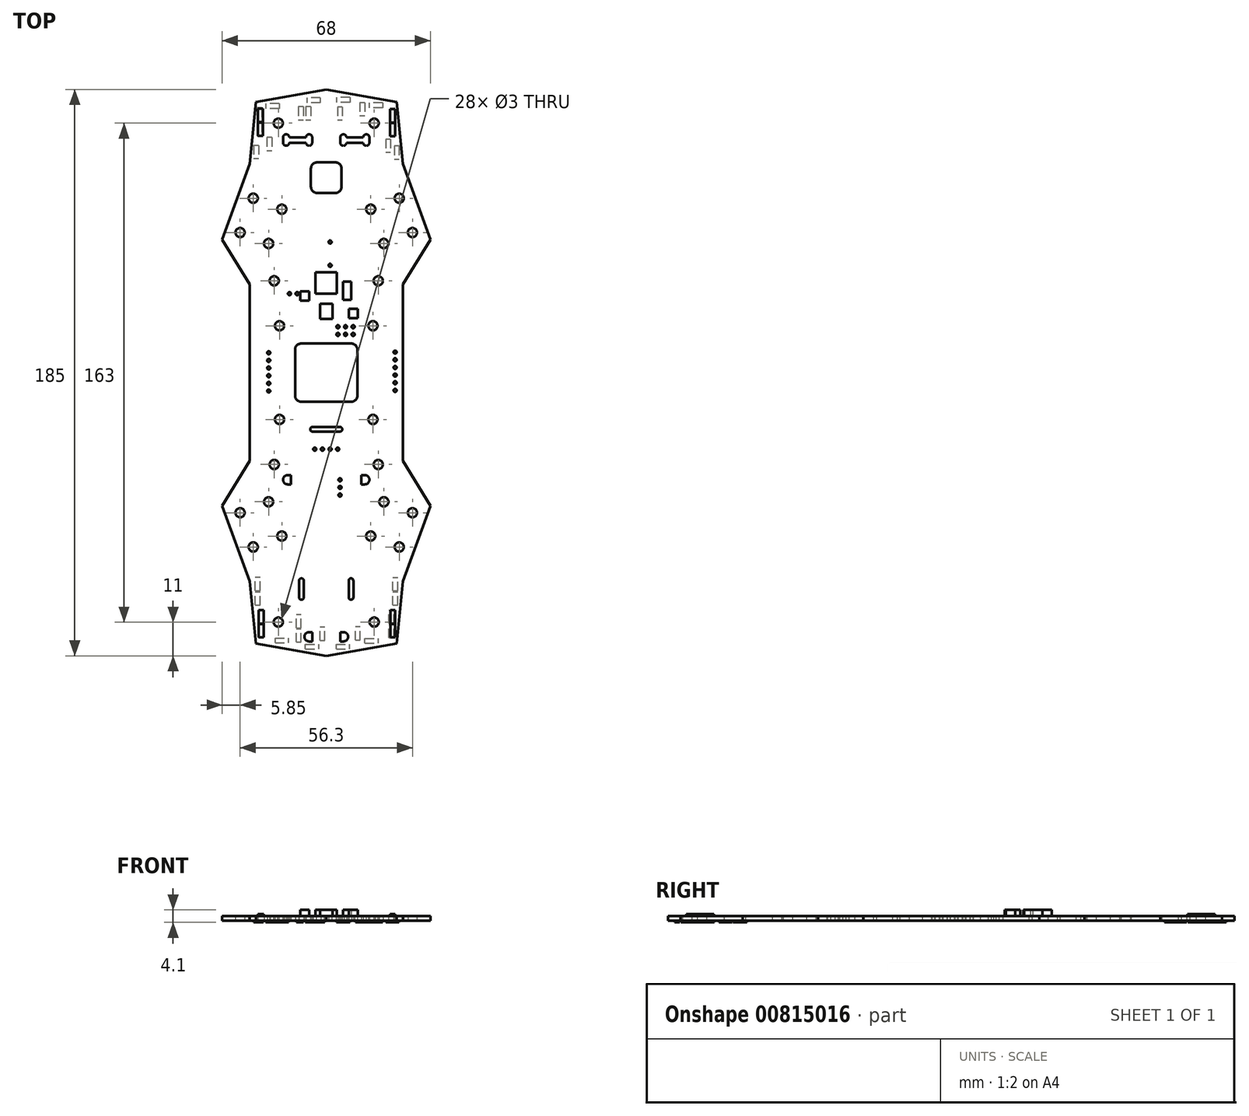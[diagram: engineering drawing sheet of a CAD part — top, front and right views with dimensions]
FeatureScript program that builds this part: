
annotation { "Feature Type Name" : "Feature", "Feature Type Description" : "" }
export const myFeature = defineFeature(function(context is Context, id is Id, definition is map)
    precondition{}
    {
        {
            var Q0;
            Q0=qCreatedBy(makeId("Top.planeOp"),FACE);
            var sketch = newSketch(context, id + "F0", { "sketchPlane" : qUnion([Q0])});
            skLineSegment(sketch, "E0.0.14", {"start": v(-25, 92.5) * mm, "end": v(-25, 63.7) * mm});
            skLineSegment(sketch, "E0.0.16", {"start": v(-25, 63.7) * mm, "end": v(-34, 49) * mm});
            skLineSegment(sketch, "E0.0.18", {"start": v(-34, 49) * mm, "end": v(-25, 24.3) * mm});
            skLineSegment(sketch, "E0.0.20", {"start": v(-25, 24.3) * mm, "end": v(-23, 4.06) * mm});
            skLineSegment(sketch, "E0.0.22", {"start": v(-23, 4.06) * mm, "end": v(0, 0) * mm});
            skLineSegment(sketch, "E0.0.23", {"start": v(0, 0) * mm, "end": v(23, 4.06) * mm});
            skLineSegment(sketch, "E0.0.25", {"start": v(23, 4.06) * mm, "end": v(25, 24.3) * mm});
            skLineSegment(sketch, "E0.0.27", {"start": v(25, 24.3) * mm, "end": v(34, 49) * mm});
            skLineSegment(sketch, "E0.0.29", {"start": v(34, 49) * mm, "end": v(25, 63.7) * mm});
            skLineSegment(sketch, "E0.0.31", {"start": v(25, 63.7) * mm, "end": v(25, 92.5) * mm});
            skLineSegment(sketch, "E1.bottom", {"start": v(34, 0) * mm, "end": v(-34, 0) * mm, "construction": true});
            skLineSegment(sketch, "E1.top", {"start": v(34, 185) * mm, "end": v(-34, 185) * mm, "construction": true});
            skLineSegment(sketch, "E1.left", {"start": v(-34, 0) * mm, "end": v(-34, 185) * mm, "construction": true});
            skLineSegment(sketch, "E1.right", {"start": v(34, 0) * mm, "end": v(34, 185) * mm, "construction": true});
            skPoint(sketch, "E2", {"position": v(0, 0) * mm});
            skLineSegment(sketch, "E3", {"start": v(0, 185) * mm, "end": v(0, 0) * mm, "construction": true});
            skLineSegment(sketch, "E4", {"start": v(-34, 92.5) * mm, "end": v(34, 92.5) * mm, "construction": true});
            skLineSegment(sketch, "E5.MirrorCS", {"start": v(-25, 92.5) * mm, "end": v(-25, 121.3) * mm});
            skLineSegment(sketch, "E6.MirrorCS", {"start": v(25, 121.3) * mm, "end": v(25, 92.5) * mm});
            skLineSegment(sketch, "E7.MirrorCS", {"start": v(34, 136) * mm, "end": v(25, 121.3) * mm});
            skLineSegment(sketch, "E8.MirrorCS", {"start": v(25, 160.7) * mm, "end": v(34, 136) * mm});
            skLineSegment(sketch, "E9.MirrorCS", {"start": v(23, 180.94) * mm, "end": v(25, 160.7) * mm});
            skLineSegment(sketch, "E10.MirrorCS", {"start": v(0, 185) * mm, "end": v(23, 180.94) * mm});
            skLineSegment(sketch, "E11.MirrorCS", {"start": v(-23, 180.94) * mm, "end": v(0, 185) * mm});
            skLineSegment(sketch, "E12.MirrorCS", {"start": v(-25, 160.7) * mm, "end": v(-23, 180.94) * mm});
            skLineSegment(sketch, "E13.MirrorCS", {"start": v(-34, 136) * mm, "end": v(-25, 160.7) * mm});
            skLineSegment(sketch, "E14.MirrorCS", {"start": v(-25, 121.3) * mm, "end": v(-34, 136) * mm});
            skPoint(sketch, "E15", {"position": v(0, 185) * mm});
            skSolve(sketch);
        }
        {
            var Q0;
            Q0 = qSketchRegion(id + "F0", true);
            extrude(context, id + "F1", {"entities" : qUnion([Q0]), "depth" : 1.5 * mm, "offsetDistance" : 25 * mm});
        }
        {
            var Q0;
            Q0=makeQuery(id+"F0.imprint","IMPRINT",FACE,{"disambiguationData":[TD([[makeQuery(id+"F0.imprint","IMPRINT",EDGE,{"derivedFrom":sQuery(id+"F0.wireOp",EDGE,"E0.0.14")}),1.0]])]});
            var sketch = newSketch(context, id + "F2", { "sketchPlane" : qUnion([Q0])});
            skLineSegment(sketch, "E16", {"start": v(0, 0) * mm, "end": v(0, 185) * mm, "construction": true});
            skLineSegment(sketch, "E17", {"start": v(61.94, 0) * mm, "end": v(-64, 0) * mm, "construction": true});
            skLineSegment(sketch, "E18", {"start": v(-46.28, 185) * mm, "end": v(44.52, 185) * mm, "construction": true});
            skPoint(sketch, "E19", {"position": v(0, 92.5) * mm});
            skLineSegment(sketch, "E20", {"start": v(-80.28, 92.5) * mm, "end": v(79, 92.5) * mm, "construction": true});
            skLineSegment(sketch, "E21.MirrorCS", {"start": v(5, 161.2) * mm, "end": v(-5, 161.2) * mm});
            skLineSegment(sketch, "E22.MirrorCS", {"start": v(-5, 161.2) * mm, "end": v(-5, 151.2) * mm});
            skLineSegment(sketch, "E23.MirrorCS", {"start": v(5, 161.2) * mm, "end": v(5, 151.2) * mm});
            skLineSegment(sketch, "E24.MirrorCS", {"start": v(5, 151.2) * mm, "end": v(-5, 151.2) * mm});
            skLineSegment(sketch, "E25.bottom", {"start": v(10.2, 83) * mm, "end": v(-10.2, 83) * mm});
            skLineSegment(sketch, "E25.top", {"start": v(10.2, 102) * mm, "end": v(-10.2, 102) * mm});
            skLineSegment(sketch, "E25.left", {"start": v(10.2, 83) * mm, "end": v(10.2, 102) * mm});
            skLineSegment(sketch, "E25.right", {"start": v(-10.2, 83) * mm, "end": v(-10.2, 102) * mm});
            skLineSegment(sketch, "E26", {"start": v(-8.1, 19.05) * mm, "end": v(-8.1, 24.55) * mm, "construction": true});
            skArc(sketch, "E27.0.startCap", {"start": v(-7.35, 19.05) * mm, "mid": v(-8.1, 18.3) * mm, "end": v(-8.85, 19.05) * mm});
            skArc(sketch, "E27.0.endCap", {"start": v(-8.85, 24.55) * mm, "mid": v(-8.1, 25.3) * mm, "end": v(-7.35, 24.55) * mm});
            skLineSegment(sketch, "E27.0.left", {"start": v(-8.85, 19.05) * mm, "end": v(-8.85, 24.55) * mm});
            skLineSegment(sketch, "E27.0.right", {"start": v(-7.35, 19.05) * mm, "end": v(-7.35, 24.55) * mm});
            skPoint(sketch, "E28", {"position": v(-8.1, 21.8) * mm});
            skLineSegment(sketch, "E29", {"start": v(-4.5, 74) * mm, "end": v(4.5, 74) * mm, "construction": true});
            skArc(sketch, "E30.0.startCap", {"start": v(-4.5, 73.25) * mm, "mid": v(-5.25, 74) * mm, "end": v(-4.5, 74.75) * mm});
            skArc(sketch, "E30.0.endCap", {"start": v(4.5, 74.75) * mm, "mid": v(5.25, 74) * mm, "end": v(4.5, 73.25) * mm});
            skLineSegment(sketch, "E30.0.left", {"start": v(-4.5, 74.75) * mm, "end": v(4.5, 74.75) * mm});
            skLineSegment(sketch, "E30.0.right", {"start": v(-4.5, 73.25) * mm, "end": v(4.5, 73.25) * mm});
            skPoint(sketch, "E31", {"position": v(0, 74) * mm});
            skArc(sketch, "E32", {"start": v(-12.6, 59) * mm, "mid": v(-14.1, 57.5) * mm, "end": v(-12.6, 56) * mm});
            skLineSegment(sketch, "E33", {"start": v(-11.5, 56) * mm, "end": v(-11.5, 59) * mm});
            skPoint(sketch, "E34", {"position": v(-11.5, 57.5) * mm});
            skLineSegment(sketch, "E35", {"start": v(-12.6, 59) * mm, "end": v(-11.5, 59) * mm});
            skLineSegment(sketch, "E36", {"start": v(-11.5, 56) * mm, "end": v(-12.6, 56) * mm});
            skArc(sketch, "E37.MirrorCS", {"start": v(12.6, 59) * mm, "mid": v(14.1, 57.5) * mm, "end": v(12.6, 56) * mm});
            skLineSegment(sketch, "E38.MirrorCS", {"start": v(11.5, 56) * mm, "end": v(12.6, 56) * mm});
            skPoint(sketch, "E39.MirrorP", {"position": v(11.5, 57.5) * mm});
            skLineSegment(sketch, "E40.MirrorCS", {"start": v(11.5, 56) * mm, "end": v(11.5, 59) * mm});
            skLineSegment(sketch, "E41.MirrorCS", {"start": v(12.6, 59) * mm, "end": v(11.5, 59) * mm});
            skArc(sketch, "E42", {"start": v(-5.65, 7.7) * mm, "mid": v(-7.15, 6.2) * mm, "end": v(-5.65, 4.7) * mm});
            skLineSegment(sketch, "E43", {"start": v(-4.55, 4.7) * mm, "end": v(-4.55, 7.7) * mm});
            skPoint(sketch, "E44", {"position": v(-4.55, 6.2) * mm});
            skLineSegment(sketch, "E45", {"start": v(-5.65, 7.7) * mm, "end": v(-4.55, 7.7) * mm});
            skLineSegment(sketch, "E46", {"start": v(-4.55, 4.7) * mm, "end": v(-5.65, 4.7) * mm});
            skPoint(sketch, "E47.MirrorP", {"position": v(4.55, 6.2) * mm});
            skLineSegment(sketch, "E48.MirrorCS", {"start": v(4.55, 4.7) * mm, "end": v(5.65, 4.7) * mm});
            skLineSegment(sketch, "E49.MirrorCS", {"start": v(5.65, 7.7) * mm, "end": v(4.55, 7.7) * mm});
            skLineSegment(sketch, "E50.MirrorCS", {"start": v(4.55, 4.7) * mm, "end": v(4.55, 7.7) * mm});
            skArc(sketch, "E51.MirrorCS", {"start": v(5.65, 7.7) * mm, "mid": v(7.15, 6.2) * mm, "end": v(5.65, 4.7) * mm});
            skCircle(sketch, "E52", {"center": v(4.5, 57.5) * mm, "radius": 0.5 * mm});
            skCircle(sketch, "E53.1.0.0", {"center": v(4.5, 55) * mm, "radius": 0.5 * mm});
            skCircle(sketch, "E53.2.0.0", {"center": v(4.5, 52.5) * mm, "radius": 0.5 * mm});
            skLineSegment(sketch, "E53.direction1", {"start": v(4.5, 57.5) * mm, "end": v(4.5, 55) * mm, "construction": true});
            skCircle(sketch, "E54", {"center": v(-18.8, 99) * mm, "radius": 0.5 * mm});
            skCircle(sketch, "E55.1.0.0", {"center": v(-18.8, 96.5) * mm, "radius": 0.5 * mm});
            skCircle(sketch, "E55.2.0.0", {"center": v(-18.8, 94) * mm, "radius": 0.5 * mm});
            skCircle(sketch, "E55.3.0.0", {"center": v(-18.8, 91.5) * mm, "radius": 0.5 * mm});
            skCircle(sketch, "E55.4.0.0", {"center": v(-18.8, 89) * mm, "radius": 0.5 * mm});
            skCircle(sketch, "E55.5.0.0", {"center": v(-18.8, 86.5) * mm, "radius": 0.5 * mm});
            skLineSegment(sketch, "E55.direction1", {"start": v(-18.8, 99) * mm, "end": v(-18.8, 96.5) * mm, "construction": true});
            skCircle(sketch, "E56", {"center": v(22.5, 99.2) * mm, "radius": 0.5 * mm});
            skCircle(sketch, "E57.1.0.0", {"center": v(22.5, 96.7) * mm, "radius": 0.5 * mm});
            skCircle(sketch, "E57.2.0.0", {"center": v(22.5, 94.2) * mm, "radius": 0.5 * mm});
            skCircle(sketch, "E57.3.0.0", {"center": v(22.5, 91.7) * mm, "radius": 0.5 * mm});
            skCircle(sketch, "E57.4.0.0", {"center": v(22.5, 89.2) * mm, "radius": 0.5 * mm});
            skCircle(sketch, "E57.5.0.0", {"center": v(22.5, 86.7) * mm, "radius": 0.5 * mm});
            skLineSegment(sketch, "E57.direction1", {"start": v(22.5, 99.2) * mm, "end": v(22.5, 96.7) * mm, "construction": true});
            skCircle(sketch, "E58", {"center": v(3.8, 107.5) * mm, "radius": 0.5 * mm});
            skCircle(sketch, "E59", {"center": v(3.8, 105) * mm, "radius": 0.5 * mm});
            skCircle(sketch, "E60.1.0.0", {"center": v(6.3, 107.5) * mm, "radius": 0.5 * mm});
            skCircle(sketch, "E60.1.0.1", {"center": v(6.3, 105) * mm, "radius": 0.5 * mm});
            skCircle(sketch, "E60.2.0.0", {"center": v(8.8, 107.5) * mm, "radius": 0.5 * mm});
            skCircle(sketch, "E60.2.0.1", {"center": v(8.8, 105) * mm, "radius": 0.5 * mm});
            skLineSegment(sketch, "E60.direction1", {"start": v(3.8, 105) * mm, "end": v(6.3, 105) * mm, "construction": true});
            skCircle(sketch, "E61", {"center": v(-12, 118.3) * mm, "radius": 0.5 * mm});
            skCircle(sketch, "E62", {"center": v(-9.5, 118.3) * mm, "radius": 0.5 * mm});
            skCircle(sketch, "E63", {"center": v(1.25, 135.18) * mm, "radius": 0.5 * mm});
            skCircle(sketch, "E64", {"center": v(1.25, 127.55) * mm, "radius": 0.5 * mm});
            skCircle(sketch, "E65", {"center": v(-3.75, 67.5) * mm, "radius": 0.5 * mm});
            skCircle(sketch, "E66.1.0.0", {"center": v(-1.25, 67.5) * mm, "radius": 0.5 * mm});
            skCircle(sketch, "E66.2.0.0", {"center": v(1.25, 67.5) * mm, "radius": 0.5 * mm});
            skCircle(sketch, "E66.3.0.0", {"center": v(3.75, 67.5) * mm, "radius": 0.5 * mm});
            skLineSegment(sketch, "E66.direction1", {"start": v(-3.75, 67.5) * mm, "end": v(-1.25, 67.5) * mm, "construction": true});
            skCircle(sketch, "E67.0", {"center": v(-15.65, 11) * mm, "radius": 1.5 * mm});
            skCircle(sketch, "E68.MirrorC", {"center": v(15.65, 11) * mm, "radius": 1.5 * mm});
            skLineSegment(sketch, "E69.MirrorCS", {"start": v(8.1, 19.05) * mm, "end": v(8.1, 24.55) * mm, "construction": true});
            skLineSegment(sketch, "E70.MirrorCS", {"start": v(7.35, 19.05) * mm, "end": v(7.35, 24.55) * mm});
            skArc(sketch, "E71.MirrorCS", {"start": v(7.35, 19.05) * mm, "mid": v(8.1, 18.3) * mm, "end": v(8.85, 19.05) * mm});
            skArc(sketch, "E72.MirrorCS", {"start": v(8.85, 24.55) * mm, "mid": v(8.1, 25.3) * mm, "end": v(7.35, 24.55) * mm});
            skPoint(sketch, "E73.MirrorP", {"position": v(8.1, 21.8) * mm});
            skLineSegment(sketch, "E74.MirrorCS", {"start": v(8.85, 19.05) * mm, "end": v(8.85, 24.55) * mm});
            skCircle(sketch, "E75.1", {"center": v(-23.85, 35.53) * mm, "radius": 1.5 * mm});
            skCircle(sketch, "E75.2", {"center": v(-28.15, 46.73) * mm, "radius": 1.5 * mm});
            skCircle(sketch, "E75.3", {"center": v(-14.51, 39.11) * mm, "radius": 1.5 * mm});
            skCircle(sketch, "E75.4", {"center": v(-18.81, 50.32) * mm, "radius": 1.5 * mm});
            skLineSegment(sketch, "E76.bottom", {"start": v(-23.85, 35.53) * mm, "end": v(-28.15, 46.73) * mm, "construction": true});
            skLineSegment(sketch, "E76.top", {"start": v(-14.51, 39.11) * mm, "end": v(-18.81, 50.32) * mm, "construction": true});
            skLineSegment(sketch, "E76.left", {"start": v(-23.85, 35.53) * mm, "end": v(-14.51, 39.11) * mm, "construction": true});
            skLineSegment(sketch, "E76.right", {"start": v(-28.15, 46.73) * mm, "end": v(-18.81, 50.32) * mm, "construction": true});
            skPoint(sketch, "E76.middle", {"position": v(-21.33, 42.92) * mm});
            skCircle(sketch, "E77.MirrorC", {"center": v(23.85, 35.53) * mm, "radius": 1.5 * mm});
            skCircle(sketch, "E78.MirrorC", {"center": v(14.51, 39.11) * mm, "radius": 1.5 * mm});
            skCircle(sketch, "E79.MirrorC", {"center": v(18.81, 50.32) * mm, "radius": 1.5 * mm});
            skCircle(sketch, "E80.MirrorC", {"center": v(28.15, 46.73) * mm, "radius": 1.5 * mm});
            skCircle(sketch, "E81.0", {"center": v(-17, 62.5) * mm, "radius": 1.5 * mm});
            skCircle(sketch, "E82", {"center": v(-15.25, 77.2) * mm, "radius": 1.5 * mm});
            skCircle(sketch, "E83.MirrorC", {"center": v(17, 62.5) * mm, "radius": 1.5 * mm});
            skCircle(sketch, "E84.MirrorC", {"center": v(15.25, 77.2) * mm, "radius": 1.5 * mm});
            skCircle(sketch, "E85.MirrorC", {"center": v(-15.25, 107.8) * mm, "radius": 1.5 * mm});
            skCircle(sketch, "E86.MirrorC", {"center": v(15.25, 107.8) * mm, "radius": 1.5 * mm});
            skCircle(sketch, "E87.MirrorC", {"center": v(-17, 122.5) * mm, "radius": 1.5 * mm});
            skCircle(sketch, "E88.MirrorC", {"center": v(17, 122.5) * mm, "radius": 1.5 * mm});
            skCircle(sketch, "E89.MirrorC", {"center": v(-28.15, 138.27) * mm, "radius": 1.5 * mm});
            skCircle(sketch, "E90.MirrorC", {"center": v(-18.81, 134.68) * mm, "radius": 1.5 * mm});
            skCircle(sketch, "E91.MirrorC", {"center": v(-14.51, 145.89) * mm, "radius": 1.5 * mm});
            skCircle(sketch, "E92.MirrorC", {"center": v(-23.85, 149.47) * mm, "radius": 1.5 * mm});
            skCircle(sketch, "E93.MirrorC", {"center": v(18.81, 134.68) * mm, "radius": 1.5 * mm});
            skCircle(sketch, "E94.MirrorC", {"center": v(28.15, 138.27) * mm, "radius": 1.5 * mm});
            skCircle(sketch, "E95.MirrorC", {"center": v(14.51, 145.89) * mm, "radius": 1.5 * mm});
            skCircle(sketch, "E96.MirrorC", {"center": v(23.85, 149.47) * mm, "radius": 1.5 * mm});
            skCircle(sketch, "E97.MirrorC", {"center": v(-15.65, 174) * mm, "radius": 1.5 * mm});
            skCircle(sketch, "E98.MirrorC", {"center": v(15.65, 174) * mm, "radius": 1.5 * mm});
            skLineSegment(sketch, "E99", {"start": v(-13.1, 169.37) * mm, "end": v(-13.1, 167.62) * mm, "construction": true});
            skArc(sketch, "E100.0.startCap", {"start": v(-14.1, 169.37) * mm, "mid": v(-13.1, 170.37) * mm, "end": v(-12.1, 169.37) * mm});
            skArc(sketch, "E100.0.endCap", {"start": v(-12.1, 167.62) * mm, "mid": v(-13.1, 166.62) * mm, "end": v(-14.1, 167.62) * mm});
            skLineSegment(sketch, "E100.0.left", {"start": v(-12.1, 169.37) * mm, "end": v(-12.1, 167.62) * mm});
            skLineSegment(sketch, "E100.0.right", {"start": v(-14.1, 169.37) * mm, "end": v(-14.1, 167.62) * mm});
            skLineSegment(sketch, "E101", {"start": v(-5.6, 169.37) * mm, "end": v(-5.6, 167.62) * mm, "construction": true});
            skArc(sketch, "E102.0.startCap", {"start": v(-6.6, 169.37) * mm, "mid": v(-5.6, 170.37) * mm, "end": v(-4.6, 169.37) * mm});
            skArc(sketch, "E102.0.endCap", {"start": v(-4.6, 167.62) * mm, "mid": v(-5.6, 166.62) * mm, "end": v(-6.6, 167.62) * mm});
            skLineSegment(sketch, "E102.0.left", {"start": v(-4.6, 169.37) * mm, "end": v(-4.6, 167.62) * mm});
            skLineSegment(sketch, "E102.0.right", {"start": v(-6.6, 169.37) * mm, "end": v(-6.6, 167.62) * mm});
            skLineSegment(sketch, "E103", {"start": v(-12.1, 169.37) * mm, "end": v(-6.6, 169.37) * mm});
            skLineSegment(sketch, "E104", {"start": v(-12.1, 167.62) * mm, "end": v(-6.6, 167.62) * mm});
            skLineSegment(sketch, "E105", {"start": v(-12.1, 167.62) * mm, "end": v(-6.6, 169.37) * mm, "construction": true});
            skPoint(sketch, "E106", {"position": v(-9.35, 168.5) * mm});
            skArc(sketch, "E107.MirrorCS", {"start": v(12.1, 167.62) * mm, "mid": v(13.1, 166.62) * mm, "end": v(14.1, 167.62) * mm});
            skLineSegment(sketch, "E108.MirrorCS", {"start": v(12.1, 167.62) * mm, "end": v(6.6, 167.62) * mm});
            skLineSegment(sketch, "E109.MirrorCS", {"start": v(12.1, 169.37) * mm, "end": v(6.6, 169.37) * mm});
            skLineSegment(sketch, "E110.MirrorCS", {"start": v(12.1, 167.62) * mm, "end": v(6.6, 169.38) * mm, "construction": true});
            skArc(sketch, "E111.MirrorCS", {"start": v(14.1, 169.37) * mm, "mid": v(13.1, 170.37) * mm, "end": v(12.1, 169.37) * mm});
            skArc(sketch, "E112.MirrorCS", {"start": v(6.6, 169.37) * mm, "mid": v(5.6, 170.37) * mm, "end": v(4.6, 169.37) * mm});
            skArc(sketch, "E113.MirrorCS", {"start": v(4.6, 167.62) * mm, "mid": v(5.6, 166.62) * mm, "end": v(6.6, 167.62) * mm});
            skLineSegment(sketch, "E114.MirrorCS", {"start": v(12.1, 169.37) * mm, "end": v(12.1, 167.62) * mm});
            skLineSegment(sketch, "E115.MirrorCS", {"start": v(5.6, 169.37) * mm, "end": v(5.6, 167.62) * mm, "construction": true});
            skPoint(sketch, "E116.MirrorP", {"position": v(9.35, 168.5) * mm});
            skLineSegment(sketch, "E117.MirrorCS", {"start": v(14.1, 169.37) * mm, "end": v(14.1, 167.62) * mm});
            skLineSegment(sketch, "E118.MirrorCS", {"start": v(6.6, 169.37) * mm, "end": v(6.6, 167.62) * mm});
            skLineSegment(sketch, "E119.MirrorCS", {"start": v(13.1, 169.37) * mm, "end": v(13.1, 167.62) * mm, "construction": true});
            skLineSegment(sketch, "E120.MirrorCS", {"start": v(4.6, 169.37) * mm, "end": v(4.6, 167.62) * mm});
            skSolve(sketch);
        }
        {
            var Q0;
            Q0 = qSketchRegion(id + "F2", true);
            extrude(context, id + "F3", {"entities" : qUnion([Q0]), "operationType" : NewBodyOperationType.REMOVE, "endBound" : BoundingType.UP_TO_NEXT, "depth" : 25 * mm, "offsetDistance" : 25 * mm});
        }
        {
            var Q0;
            Q0=makeQuery(id+"F2.imprint","IMPRINT",FACE,{"disambiguationData":[TD([[makeQuery(id+"F2.imprint","IMPRINT",EDGE,{"derivedFrom":sQuery(id+"F2.wireOp",EDGE,"E21.MirrorCS")}),-1.0]])]});
            var sketch = newSketch(context, id + "F4", { "sketchPlane" : qUnion([Q0])});
            skLineSegment(sketch, "E121.bottom", {"start": v(-22.1, 5.88) * mm, "end": v(-20.5, 5.88) * mm});
            skLineSegment(sketch, "E121.top", {"start": v(-22.1, 10.28) * mm, "end": v(-20.5, 10.28) * mm});
            skLineSegment(sketch, "E121.left", {"start": v(-22.1, 5.88) * mm, "end": v(-22.1, 10.28) * mm});
            skLineSegment(sketch, "E121.right", {"start": v(-20.5, 5.88) * mm, "end": v(-20.5, 10.28) * mm});
            skLineSegment(sketch, "E122", {"start": v(-22.1, 5.88) * mm, "end": v(-20.5, 10.28) * mm, "construction": true});
            skPoint(sketch, "E123", {"position": v(-21.3, 8.08) * mm});
            skLineSegment(sketch, "E124.bottom", {"start": v(-22.1, 10.69) * mm, "end": v(-20.5, 10.69) * mm});
            skLineSegment(sketch, "E124.top", {"start": v(-22.1, 15.09) * mm, "end": v(-20.5, 15.09) * mm});
            skLineSegment(sketch, "E124.left", {"start": v(-22.1, 10.69) * mm, "end": v(-22.1, 15.09) * mm});
            skLineSegment(sketch, "E124.right", {"start": v(-20.5, 10.69) * mm, "end": v(-20.5, 15.09) * mm});
            skLineSegment(sketch, "E125", {"start": v(-22.1, 10.69) * mm, "end": v(-20.5, 15.09) * mm, "construction": true});
            skPoint(sketch, "E126", {"position": v(-21.3, 12.89) * mm});
            skLineSegment(sketch, "E127.bottom", {"start": v(-23.2, 16.56) * mm, "end": v(-21.6, 16.56) * mm});
            skLineSegment(sketch, "E127.top", {"start": v(-23.2, 20.96) * mm, "end": v(-21.6, 20.96) * mm});
            skLineSegment(sketch, "E127.left", {"start": v(-23.2, 16.56) * mm, "end": v(-23.2, 20.96) * mm});
            skLineSegment(sketch, "E127.right", {"start": v(-21.6, 16.56) * mm, "end": v(-21.6, 20.96) * mm});
            skLineSegment(sketch, "E128", {"start": v(-23.2, 16.56) * mm, "end": v(-21.6, 20.96) * mm, "construction": true});
            skPoint(sketch, "E129", {"position": v(-22.4, 18.76) * mm});
            skLineSegment(sketch, "E130.bottom", {"start": v(-23.2, 21.3) * mm, "end": v(-21.6, 21.3) * mm});
            skLineSegment(sketch, "E130.top", {"start": v(-23.2, 25.7) * mm, "end": v(-21.6, 25.7) * mm});
            skLineSegment(sketch, "E130.left", {"start": v(-23.2, 21.3) * mm, "end": v(-23.2, 25.7) * mm});
            skLineSegment(sketch, "E130.right", {"start": v(-21.6, 21.3) * mm, "end": v(-21.6, 25.7) * mm});
            skLineSegment(sketch, "E131", {"start": v(-23.2, 21.3) * mm, "end": v(-21.6, 25.7) * mm, "construction": true});
            skPoint(sketch, "E132", {"position": v(-22.4, 23.5) * mm});
            skLineSegment(sketch, "E133.bottom", {"start": v(9.5, 5.13) * mm, "end": v(11.1, 5.13) * mm});
            skLineSegment(sketch, "E133.top", {"start": v(9.5, 9.53) * mm, "end": v(11.1, 9.53) * mm});
            skLineSegment(sketch, "E133.left", {"start": v(9.5, 5.13) * mm, "end": v(9.5, 9.53) * mm});
            skLineSegment(sketch, "E133.right", {"start": v(11.1, 5.13) * mm, "end": v(11.1, 9.53) * mm});
            skLineSegment(sketch, "E134", {"start": v(9.5, 5.13) * mm, "end": v(11.1, 9.53) * mm, "construction": true});
            skPoint(sketch, "E135", {"position": v(10.3, 7.33) * mm});
            skLineSegment(sketch, "E136.bottom", {"start": v(-2.06, 5.03) * mm, "end": v(-0.46, 5.03) * mm});
            skLineSegment(sketch, "E136.top", {"start": v(-2.06, 9.43) * mm, "end": v(-0.46, 9.43) * mm});
            skLineSegment(sketch, "E136.left", {"start": v(-2.06, 5.03) * mm, "end": v(-2.06, 9.43) * mm});
            skLineSegment(sketch, "E136.right", {"start": v(-0.46, 5.03) * mm, "end": v(-0.46, 9.43) * mm});
            skLineSegment(sketch, "E137", {"start": v(-2.06, 5.03) * mm, "end": v(-0.46, 9.43) * mm, "construction": true});
            skPoint(sketch, "E138", {"position": v(-1.26, 7.23) * mm});
            skLineSegment(sketch, "E139.bottom", {"start": v(-9.8, 4.5) * mm, "end": v(-8.2, 4.5) * mm});
            skLineSegment(sketch, "E139.top", {"start": v(-9.8, 8.9) * mm, "end": v(-8.2, 8.9) * mm});
            skLineSegment(sketch, "E139.left", {"start": v(-9.8, 4.5) * mm, "end": v(-9.8, 8.9) * mm});
            skLineSegment(sketch, "E139.right", {"start": v(-8.2, 4.5) * mm, "end": v(-8.2, 8.9) * mm});
            skLineSegment(sketch, "E140", {"start": v(-9.8, 4.5) * mm, "end": v(-8.2, 8.9) * mm, "construction": true});
            skPoint(sketch, "E141", {"position": v(-9, 6.7) * mm});
            skLineSegment(sketch, "E142.bottom", {"start": v(-9.8, 9.1) * mm, "end": v(-8.2, 9.1) * mm});
            skLineSegment(sketch, "E142.top", {"start": v(-9.8, 13.5) * mm, "end": v(-8.2, 13.5) * mm});
            skLineSegment(sketch, "E142.left", {"start": v(-9.8, 9.1) * mm, "end": v(-9.8, 13.5) * mm});
            skLineSegment(sketch, "E142.right", {"start": v(-8.2, 9.1) * mm, "end": v(-8.2, 13.5) * mm});
            skLineSegment(sketch, "E143", {"start": v(-9.8, 9.1) * mm, "end": v(-8.2, 13.5) * mm, "construction": true});
            skPoint(sketch, "E144", {"position": v(-9, 11.3) * mm});
            skLineSegment(sketch, "E145.bottom", {"start": v(20.49, 5.88) * mm, "end": v(22.09, 5.88) * mm});
            skLineSegment(sketch, "E145.top", {"start": v(20.49, 10.28) * mm, "end": v(22.09, 10.28) * mm});
            skLineSegment(sketch, "E145.left", {"start": v(20.49, 5.88) * mm, "end": v(20.49, 10.28) * mm});
            skLineSegment(sketch, "E145.right", {"start": v(22.09, 5.88) * mm, "end": v(22.09, 10.28) * mm});
            skLineSegment(sketch, "E146", {"start": v(20.49, 5.88) * mm, "end": v(22.09, 10.28) * mm, "construction": true});
            skPoint(sketch, "E147", {"position": v(21.29, 8.08) * mm});
            skLineSegment(sketch, "E148.bottom", {"start": v(20.49, 10.58) * mm, "end": v(22.09, 10.58) * mm});
            skLineSegment(sketch, "E148.top", {"start": v(20.49, 14.98) * mm, "end": v(22.09, 14.98) * mm});
            skLineSegment(sketch, "E148.left", {"start": v(20.49, 10.58) * mm, "end": v(20.49, 14.98) * mm});
            skLineSegment(sketch, "E148.right", {"start": v(22.09, 10.58) * mm, "end": v(22.09, 14.98) * mm});
            skLineSegment(sketch, "E149", {"start": v(20.49, 10.58) * mm, "end": v(22.09, 14.98) * mm, "construction": true});
            skPoint(sketch, "E150", {"position": v(21.29, 12.78) * mm});
            skLineSegment(sketch, "E151.bottom", {"start": v(21.75, 16.56) * mm, "end": v(23.35, 16.56) * mm});
            skLineSegment(sketch, "E151.top", {"start": v(21.75, 20.96) * mm, "end": v(23.35, 20.96) * mm});
            skLineSegment(sketch, "E151.left", {"start": v(21.75, 16.56) * mm, "end": v(21.75, 20.96) * mm});
            skLineSegment(sketch, "E151.right", {"start": v(23.35, 16.56) * mm, "end": v(23.35, 20.96) * mm});
            skLineSegment(sketch, "E152", {"start": v(21.75, 16.56) * mm, "end": v(23.35, 20.96) * mm, "construction": true});
            skPoint(sketch, "E153", {"position": v(22.55, 18.76) * mm});
            skLineSegment(sketch, "E154.bottom", {"start": v(21.75, 21.22) * mm, "end": v(23.35, 21.22) * mm});
            skLineSegment(sketch, "E154.top", {"start": v(21.75, 25.62) * mm, "end": v(23.35, 25.62) * mm});
            skLineSegment(sketch, "E154.left", {"start": v(21.75, 21.22) * mm, "end": v(21.75, 25.62) * mm});
            skLineSegment(sketch, "E154.right", {"start": v(23.35, 21.22) * mm, "end": v(23.35, 25.62) * mm});
            skLineSegment(sketch, "E155", {"start": v(21.75, 21.22) * mm, "end": v(23.35, 25.62) * mm, "construction": true});
            skPoint(sketch, "E156", {"position": v(22.55, 23.42) * mm});
            skLineSegment(sketch, "E157.bottom", {"start": v(-16.66, 4.2) * mm, "end": v(-12.26, 4.2) * mm});
            skLineSegment(sketch, "E157.top", {"start": v(-16.66, 5.8) * mm, "end": v(-12.26, 5.8) * mm});
            skLineSegment(sketch, "E157.left", {"start": v(-16.66, 4.2) * mm, "end": v(-16.66, 5.8) * mm});
            skLineSegment(sketch, "E157.right", {"start": v(-12.26, 4.2) * mm, "end": v(-12.26, 5.8) * mm});
            skLineSegment(sketch, "E158", {"start": v(-16.66, 4.2) * mm, "end": v(-12.26, 5.8) * mm, "construction": true});
            skPoint(sketch, "E159", {"position": v(-14.46, 5) * mm});
            skLineSegment(sketch, "E160.bottom", {"start": v(-6.84, 2.16) * mm, "end": v(-2.44, 2.16) * mm});
            skLineSegment(sketch, "E160.top", {"start": v(-6.84, 3.76) * mm, "end": v(-2.44, 3.76) * mm});
            skLineSegment(sketch, "E160.left", {"start": v(-6.84, 2.16) * mm, "end": v(-6.84, 3.76) * mm});
            skLineSegment(sketch, "E160.right", {"start": v(-2.44, 2.16) * mm, "end": v(-2.44, 3.76) * mm});
            skLineSegment(sketch, "E161", {"start": v(-6.84, 2.16) * mm, "end": v(-2.44, 3.76) * mm, "construction": true});
            skPoint(sketch, "E162", {"position": v(-4.64, 2.96) * mm});
            skLineSegment(sketch, "E163.bottom", {"start": v(3.28, 2.16) * mm, "end": v(7.68, 2.16) * mm});
            skLineSegment(sketch, "E163.top", {"start": v(3.28, 3.76) * mm, "end": v(7.68, 3.76) * mm});
            skLineSegment(sketch, "E163.left", {"start": v(3.28, 2.16) * mm, "end": v(3.28, 3.76) * mm});
            skLineSegment(sketch, "E163.right", {"start": v(7.68, 2.16) * mm, "end": v(7.68, 3.76) * mm});
            skLineSegment(sketch, "E164", {"start": v(3.28, 2.16) * mm, "end": v(7.68, 3.76) * mm, "construction": true});
            skPoint(sketch, "E165", {"position": v(5.48, 2.96) * mm});
            skLineSegment(sketch, "E166.bottom", {"start": v(12.61, 4.1) * mm, "end": v(17.01, 4.1) * mm});
            skLineSegment(sketch, "E166.top", {"start": v(12.61, 5.7) * mm, "end": v(17.01, 5.7) * mm});
            skLineSegment(sketch, "E166.left", {"start": v(12.61, 4.1) * mm, "end": v(12.61, 5.7) * mm});
            skLineSegment(sketch, "E166.right", {"start": v(17.01, 4.1) * mm, "end": v(17.01, 5.7) * mm});
            skLineSegment(sketch, "E167", {"start": v(12.61, 4.1) * mm, "end": v(17.01, 5.7) * mm, "construction": true});
            skPoint(sketch, "E168", {"position": v(14.81, 4.9) * mm});
            skLineSegment(sketch, "E169.bottom", {"start": v(22.4, 178.65) * mm, "end": v(20.8, 178.65) * mm});
            skLineSegment(sketch, "E169.top", {"start": v(22.4, 174.25) * mm, "end": v(20.8, 174.25) * mm});
            skLineSegment(sketch, "E169.left", {"start": v(22.4, 178.65) * mm, "end": v(22.4, 174.25) * mm});
            skLineSegment(sketch, "E169.right", {"start": v(20.8, 178.65) * mm, "end": v(20.8, 174.25) * mm});
            skLineSegment(sketch, "E170", {"start": v(22.4, 178.65) * mm, "end": v(20.8, 174.25) * mm, "construction": true});
            skPoint(sketch, "E171", {"position": v(21.6, 176.45) * mm});
            skLineSegment(sketch, "E172.bottom", {"start": v(22.4, 174.23) * mm, "end": v(20.8, 174.23) * mm});
            skLineSegment(sketch, "E172.top", {"start": v(22.4, 169.83) * mm, "end": v(20.8, 169.83) * mm});
            skLineSegment(sketch, "E172.left", {"start": v(22.4, 174.23) * mm, "end": v(22.4, 169.83) * mm});
            skLineSegment(sketch, "E172.right", {"start": v(20.8, 174.23) * mm, "end": v(20.8, 169.83) * mm});
            skLineSegment(sketch, "E173", {"start": v(22.4, 174.23) * mm, "end": v(20.8, 169.83) * mm, "construction": true});
            skPoint(sketch, "E174", {"position": v(21.6, 172.03) * mm});
            skLineSegment(sketch, "E175.bottom", {"start": v(20.99, 168.78) * mm, "end": v(19.39, 168.78) * mm});
            skLineSegment(sketch, "E175.top", {"start": v(20.99, 164.38) * mm, "end": v(19.39, 164.38) * mm});
            skLineSegment(sketch, "E175.left", {"start": v(20.99, 168.78) * mm, "end": v(20.99, 164.38) * mm});
            skLineSegment(sketch, "E175.right", {"start": v(19.39, 168.78) * mm, "end": v(19.39, 164.38) * mm});
            skLineSegment(sketch, "E176", {"start": v(20.99, 168.78) * mm, "end": v(19.39, 164.38) * mm, "construction": true});
            skPoint(sketch, "E177", {"position": v(20.19, 166.58) * mm});
            skLineSegment(sketch, "E178.bottom", {"start": v(23.82, 166.52) * mm, "end": v(22.22, 166.52) * mm});
            skLineSegment(sketch, "E178.top", {"start": v(23.82, 162.12) * mm, "end": v(22.22, 162.12) * mm});
            skLineSegment(sketch, "E178.left", {"start": v(23.82, 166.52) * mm, "end": v(23.82, 162.12) * mm});
            skLineSegment(sketch, "E178.right", {"start": v(22.22, 166.52) * mm, "end": v(22.22, 162.12) * mm});
            skLineSegment(sketch, "E179", {"start": v(23.82, 166.52) * mm, "end": v(22.22, 162.12) * mm, "construction": true});
            skPoint(sketch, "E180", {"position": v(23.02, 164.32) * mm});
            skLineSegment(sketch, "E181.bottom", {"start": v(12.6, 180.7) * mm, "end": v(11, 180.7) * mm});
            skLineSegment(sketch, "E181.top", {"start": v(12.6, 176.3) * mm, "end": v(11, 176.3) * mm});
            skLineSegment(sketch, "E181.left", {"start": v(12.6, 180.7) * mm, "end": v(12.6, 176.3) * mm});
            skLineSegment(sketch, "E181.right", {"start": v(11, 180.7) * mm, "end": v(11, 176.3) * mm});
            skLineSegment(sketch, "E182", {"start": v(12.6, 180.7) * mm, "end": v(11, 176.3) * mm, "construction": true});
            skPoint(sketch, "E183", {"position": v(11.8, 178.5) * mm});
            skLineSegment(sketch, "E184.bottom", {"start": v(5.28, 179.33) * mm, "end": v(3.68, 179.33) * mm});
            skLineSegment(sketch, "E184.top", {"start": v(5.28, 174.93) * mm, "end": v(3.68, 174.93) * mm});
            skLineSegment(sketch, "E184.left", {"start": v(5.28, 179.33) * mm, "end": v(5.28, 174.93) * mm});
            skLineSegment(sketch, "E184.right", {"start": v(3.68, 179.33) * mm, "end": v(3.68, 174.93) * mm});
            skLineSegment(sketch, "E185", {"start": v(5.28, 179.33) * mm, "end": v(3.68, 174.93) * mm, "construction": true});
            skPoint(sketch, "E186", {"position": v(4.48, 177.13) * mm});
            skLineSegment(sketch, "E187.bottom", {"start": v(-7.5, 179.37) * mm, "end": v(-9.1, 179.37) * mm});
            skLineSegment(sketch, "E187.top", {"start": v(-7.5, 174.97) * mm, "end": v(-9.1, 174.97) * mm});
            skLineSegment(sketch, "E187.left", {"start": v(-7.5, 179.37) * mm, "end": v(-7.5, 174.97) * mm});
            skLineSegment(sketch, "E187.right", {"start": v(-9.1, 179.37) * mm, "end": v(-9.1, 174.97) * mm});
            skLineSegment(sketch, "E188", {"start": v(-7.5, 179.37) * mm, "end": v(-9.1, 174.97) * mm, "construction": true});
            skPoint(sketch, "E189", {"position": v(-8.3, 177.17) * mm});
            skLineSegment(sketch, "E190.bottom", {"start": v(-5.11, 179.37) * mm, "end": v(-6.71, 179.37) * mm});
            skLineSegment(sketch, "E190.top", {"start": v(-5.11, 174.97) * mm, "end": v(-6.71, 174.97) * mm});
            skLineSegment(sketch, "E190.left", {"start": v(-5.11, 179.37) * mm, "end": v(-5.11, 174.97) * mm});
            skLineSegment(sketch, "E190.right", {"start": v(-6.71, 179.37) * mm, "end": v(-6.71, 174.97) * mm});
            skLineSegment(sketch, "E191", {"start": v(-5.11, 179.37) * mm, "end": v(-6.71, 174.97) * mm, "construction": true});
            skPoint(sketch, "E192", {"position": v(-5.91, 177.17) * mm});
            skLineSegment(sketch, "E193.bottom", {"start": v(-21.04, 179) * mm, "end": v(-22.64, 179) * mm});
            skLineSegment(sketch, "E193.top", {"start": v(-21.04, 174.6) * mm, "end": v(-22.64, 174.6) * mm});
            skLineSegment(sketch, "E193.left", {"start": v(-21.04, 179) * mm, "end": v(-21.04, 174.6) * mm});
            skLineSegment(sketch, "E193.right", {"start": v(-22.64, 179) * mm, "end": v(-22.64, 174.6) * mm});
            skLineSegment(sketch, "E194", {"start": v(-21.04, 179) * mm, "end": v(-22.64, 174.6) * mm, "construction": true});
            skPoint(sketch, "E195", {"position": v(-21.84, 176.8) * mm});
            skLineSegment(sketch, "E196.bottom", {"start": v(-21.04, 174.18) * mm, "end": v(-22.64, 174.18) * mm});
            skLineSegment(sketch, "E196.top", {"start": v(-21.04, 169.78) * mm, "end": v(-22.64, 169.78) * mm});
            skLineSegment(sketch, "E196.left", {"start": v(-21.04, 174.18) * mm, "end": v(-21.04, 169.78) * mm});
            skLineSegment(sketch, "E196.right", {"start": v(-22.64, 174.18) * mm, "end": v(-22.64, 169.78) * mm});
            skLineSegment(sketch, "E197", {"start": v(-21.04, 174.18) * mm, "end": v(-22.64, 169.78) * mm, "construction": true});
            skPoint(sketch, "E198", {"position": v(-21.84, 171.98) * mm});
            skLineSegment(sketch, "E199.bottom", {"start": v(-17.81, 169.35) * mm, "end": v(-19.41, 169.35) * mm});
            skLineSegment(sketch, "E199.top", {"start": v(-17.81, 164.95) * mm, "end": v(-19.41, 164.95) * mm});
            skLineSegment(sketch, "E199.left", {"start": v(-17.81, 169.35) * mm, "end": v(-17.81, 164.95) * mm});
            skLineSegment(sketch, "E199.right", {"start": v(-19.41, 169.35) * mm, "end": v(-19.41, 164.95) * mm});
            skLineSegment(sketch, "E200", {"start": v(-17.81, 169.35) * mm, "end": v(-19.41, 164.95) * mm, "construction": true});
            skPoint(sketch, "E201", {"position": v(-18.61, 167.15) * mm});
            skLineSegment(sketch, "E202.bottom", {"start": v(-22.1, 166.74) * mm, "end": v(-23.7, 166.74) * mm});
            skLineSegment(sketch, "E202.top", {"start": v(-22.1, 162.34) * mm, "end": v(-23.7, 162.34) * mm});
            skLineSegment(sketch, "E202.left", {"start": v(-22.1, 166.74) * mm, "end": v(-22.1, 162.34) * mm});
            skLineSegment(sketch, "E202.right", {"start": v(-23.7, 166.74) * mm, "end": v(-23.7, 162.34) * mm});
            skLineSegment(sketch, "E203", {"start": v(-22.1, 166.74) * mm, "end": v(-23.7, 162.34) * mm, "construction": true});
            skPoint(sketch, "E204", {"position": v(-22.9, 164.54) * mm});
            skLineSegment(sketch, "E205.bottom", {"start": v(18.44, 180.67) * mm, "end": v(14.04, 180.67) * mm});
            skLineSegment(sketch, "E205.top", {"start": v(18.44, 179.07) * mm, "end": v(14.04, 179.07) * mm});
            skLineSegment(sketch, "E205.left", {"start": v(18.44, 180.67) * mm, "end": v(18.44, 179.07) * mm});
            skLineSegment(sketch, "E205.right", {"start": v(14.04, 180.67) * mm, "end": v(14.04, 179.07) * mm});
            skLineSegment(sketch, "E206", {"start": v(18.44, 180.67) * mm, "end": v(14.04, 179.07) * mm, "construction": true});
            skPoint(sketch, "E207", {"position": v(16.24, 179.87) * mm});
            skLineSegment(sketch, "E208.bottom", {"start": v(7.77, 182.38) * mm, "end": v(3.37, 182.38) * mm});
            skLineSegment(sketch, "E208.top", {"start": v(7.77, 180.78) * mm, "end": v(3.37, 180.78) * mm});
            skLineSegment(sketch, "E208.left", {"start": v(7.77, 182.38) * mm, "end": v(7.77, 180.78) * mm});
            skLineSegment(sketch, "E208.right", {"start": v(3.37, 182.38) * mm, "end": v(3.37, 180.78) * mm});
            skLineSegment(sketch, "E209", {"start": v(7.77, 182.38) * mm, "end": v(3.37, 180.78) * mm, "construction": true});
            skPoint(sketch, "E210", {"position": v(5.57, 181.58) * mm});
            skLineSegment(sketch, "E211.bottom", {"start": v(-1.96, 182.3) * mm, "end": v(-6.36, 182.3) * mm});
            skLineSegment(sketch, "E211.top", {"start": v(-1.96, 180.7) * mm, "end": v(-6.36, 180.7) * mm});
            skLineSegment(sketch, "E211.left", {"start": v(-1.96, 182.3) * mm, "end": v(-1.96, 180.7) * mm});
            skLineSegment(sketch, "E211.right", {"start": v(-6.36, 182.3) * mm, "end": v(-6.36, 180.7) * mm});
            skLineSegment(sketch, "E212", {"start": v(-1.96, 182.3) * mm, "end": v(-6.36, 180.7) * mm, "construction": true});
            skPoint(sketch, "E213", {"position": v(-4.16, 181.5) * mm});
            skLineSegment(sketch, "E214.bottom", {"start": v(-15.37, 180.35) * mm, "end": v(-19.77, 180.35) * mm});
            skLineSegment(sketch, "E214.top", {"start": v(-15.37, 178.75) * mm, "end": v(-19.77, 178.75) * mm});
            skLineSegment(sketch, "E214.left", {"start": v(-15.37, 180.35) * mm, "end": v(-15.37, 178.75) * mm});
            skLineSegment(sketch, "E214.right", {"start": v(-19.77, 180.35) * mm, "end": v(-19.77, 178.75) * mm});
            skLineSegment(sketch, "E215", {"start": v(-15.37, 180.35) * mm, "end": v(-19.77, 178.75) * mm, "construction": true});
            skPoint(sketch, "E216", {"position": v(-17.57, 179.55) * mm});
            skSolve(sketch);
        }
        {
            var Q0;
            Q0 = qSketchRegion(id + "F4", true);
            extrude(context, id + "F5", {"entities" : qUnion([Q0]), "oppositeDirection" : true, "depth" : .6 * mm, "offsetDistance" : 25 * mm});
        }
        {
            var Q0;
            Q0=makeQuery(id+"F1.opExtrude","SWEPT_EDGE",EDGE,{"disambiguationData":[OSD([sQuery(id+"F0.wireOp",EDGE,"04b0d970-0c2d-43c9-a8c2-f805e1ce5058.0.27"),sQuery(id+"F0.wireOp",EDGE,"04b0d970-0c2d-43c9-a8c2-f805e1ce5058.0.29")])]});
            var Q1;
            Q1=makeQuery(id+"F1.opExtrude","SWEPT_EDGE",EDGE,{"disambiguationData":[OSD([sQuery(id+"F0.wireOp",EDGE,"04b0d970-0c2d-43c9-a8c2-f805e1ce5058.0.29"),sQuery(id+"F0.wireOp",EDGE,"04b0d970-0c2d-43c9-a8c2-f805e1ce5058.0.31")])]});
            var Q2;
            Q2=makeQuery(id+"F1.opExtrude","SWEPT_EDGE",EDGE,{"disambiguationData":[OSD([sQuery(id+"F0.wireOp",EDGE,"04b0d970-0c2d-43c9-a8c2-f805e1ce5058.0.25"),sQuery(id+"F0.wireOp",EDGE,"04b0d970-0c2d-43c9-a8c2-f805e1ce5058.0.27")])]});
            var Q3;
            Q3=makeQuery(id+"F1.opExtrude","SWEPT_EDGE",EDGE,{"disambiguationData":[OSD([sQuery(id+"F0.wireOp",EDGE,"04b0d970-0c2d-43c9-a8c2-f805e1ce5058.0.31"),sQuery(id+"F0.wireOp",EDGE,"04b0d970-0c2d-43c9-a8c2-f805e1ce5058.0.33")])]});
            var Q4;
            Q4=makeQuery(id+"F1.opExtrude","SWEPT_EDGE",EDGE,{"disambiguationData":[OSD([sQuery(id+"F0.wireOp",EDGE,"04b0d970-0c2d-43c9-a8c2-f805e1ce5058.0.1"),sQuery(id+"F0.wireOp",EDGE,"04b0d970-0c2d-43c9-a8c2-f805e1ce5058.0.33")])]});
            var Q5;
            Q5=makeQuery(id+"F1.opExtrude","SWEPT_EDGE",EDGE,{"disambiguationData":[OSD([sQuery(id+"F0.wireOp",EDGE,"04b0d970-0c2d-43c9-a8c2-f805e1ce5058.0.1"),sQuery(id+"F0.wireOp",EDGE,"04b0d970-0c2d-43c9-a8c2-f805e1ce5058.0.3")])]});
            var Q6;
            Q6=makeQuery(id+"F1.opExtrude","SWEPT_EDGE",EDGE,{"disambiguationData":[OSD([sQuery(id+"F0.wireOp",EDGE,"04b0d970-0c2d-43c9-a8c2-f805e1ce5058.0.3"),sQuery(id+"F0.wireOp",EDGE,"04b0d970-0c2d-43c9-a8c2-f805e1ce5058.0.5")])]});
            var Q7;
            Q7=makeQuery(id+"F1.opExtrude","SWEPT_EDGE",EDGE,{"disambiguationData":[OSD([sQuery(id+"F0.wireOp",EDGE,"04b0d970-0c2d-43c9-a8c2-f805e1ce5058.0.6"),sQuery(id+"F0.wireOp",EDGE,"04b0d970-0c2d-43c9-a8c2-f805e1ce5058.0.8")])]});
            var Q8;
            Q8=makeQuery(id+"F1.opExtrude","SWEPT_EDGE",EDGE,{"disambiguationData":[OSD([sQuery(id+"F0.wireOp",EDGE,"04b0d970-0c2d-43c9-a8c2-f805e1ce5058.0.8"),sQuery(id+"F0.wireOp",EDGE,"04b0d970-0c2d-43c9-a8c2-f805e1ce5058.0.10")])]});
            var Q9;
            Q9=makeQuery(id+"F1.opExtrude","SWEPT_EDGE",EDGE,{"disambiguationData":[OSD([sQuery(id+"F0.wireOp",EDGE,"04b0d970-0c2d-43c9-a8c2-f805e1ce5058.0.10"),sQuery(id+"F0.wireOp",EDGE,"04b0d970-0c2d-43c9-a8c2-f805e1ce5058.0.12")])]});
            var Q10;
            Q10=makeQuery(id+"F1.opExtrude","SWEPT_EDGE",EDGE,{"disambiguationData":[OSD([sQuery(id+"F0.wireOp",EDGE,"04b0d970-0c2d-43c9-a8c2-f805e1ce5058.0.12"),sQuery(id+"F0.wireOp",EDGE,"04b0d970-0c2d-43c9-a8c2-f805e1ce5058.0.14")])]});
            var Q11;
            Q11=makeQuery(id+"F1.opExtrude","SWEPT_EDGE",EDGE,{"disambiguationData":[OSD([sQuery(id+"F0.wireOp",EDGE,"04b0d970-0c2d-43c9-a8c2-f805e1ce5058.0.14"),sQuery(id+"F0.wireOp",EDGE,"04b0d970-0c2d-43c9-a8c2-f805e1ce5058.0.16")])]});
            var Q12;
            Q12=makeQuery(id+"F1.opExtrude","SWEPT_EDGE",EDGE,{"disambiguationData":[OSD([sQuery(id+"F0.wireOp",EDGE,"04b0d970-0c2d-43c9-a8c2-f805e1ce5058.0.16"),sQuery(id+"F0.wireOp",EDGE,"04b0d970-0c2d-43c9-a8c2-f805e1ce5058.0.18")])]});
            var Q13;
            Q13=makeQuery(id+"F1.opExtrude","SWEPT_EDGE",EDGE,{"disambiguationData":[OSD([sQuery(id+"F0.wireOp",EDGE,"04b0d970-0c2d-43c9-a8c2-f805e1ce5058.0.18"),sQuery(id+"F0.wireOp",EDGE,"04b0d970-0c2d-43c9-a8c2-f805e1ce5058.0.20")])]});
            var Q14;
            Q14=makeQuery(id+"F1.opExtrude","SWEPT_EDGE",EDGE,{"disambiguationData":[OSD([sQuery(id+"F0.wireOp",EDGE,"04b0d970-0c2d-43c9-a8c2-f805e1ce5058.0.20"),sQuery(id+"F0.wireOp",EDGE,"04b0d970-0c2d-43c9-a8c2-f805e1ce5058.0.22")])]});
            var Q15;
            Q15=makeQuery(id+"F1.opExtrude","SWEPT_EDGE",EDGE,{"disambiguationData":[OSD([sQuery(id+"F0.wireOp",EDGE,"04b0d970-0c2d-43c9-a8c2-f805e1ce5058.0.23"),sQuery(id+"F0.wireOp",EDGE,"04b0d970-0c2d-43c9-a8c2-f805e1ce5058.0.25")])]});
            var Q16;
            Q16=makeQuery(id+"F3.boolean.opBoolean","COPY",EDGE,{"derivedFrom":makeQuery(id+"F3.opExtrude","SWEPT_EDGE",EDGE,{"disambiguationData":[OSD([sQuery(id+"F2.wireOp",EDGE,"98604dad-a57c-4539-978a-768864eea020.bottom"),sQuery(id+"F2.wireOp",EDGE,"98604dad-a57c-4539-978a-768864eea020.right")])]})});
            var Q17;
            Q17=makeQuery(id+"F3.boolean.opBoolean","COPY",EDGE,{"derivedFrom":makeQuery(id+"F3.opExtrude","SWEPT_EDGE",EDGE,{"disambiguationData":[OSD([sQuery(id+"F2.wireOp",EDGE,"98604dad-a57c-4539-978a-768864eea020.top"),sQuery(id+"F2.wireOp",EDGE,"98604dad-a57c-4539-978a-768864eea020.left")])]})});
            var Q18;
            Q18=makeQuery(id+"F3.boolean.opBoolean","COPY",EDGE,{"derivedFrom":makeQuery(id+"F3.opExtrude","SWEPT_EDGE",EDGE,{"disambiguationData":[OSD([sQuery(id+"F2.wireOp",EDGE,"98604dad-a57c-4539-978a-768864eea020.bottom"),sQuery(id+"F2.wireOp",EDGE,"98604dad-a57c-4539-978a-768864eea020.left")])]})});
            var Q19;
            Q19=makeQuery(id+"F3.boolean.opBoolean","COPY",EDGE,{"derivedFrom":makeQuery(id+"F3.opExtrude","SWEPT_EDGE",EDGE,{"disambiguationData":[OSD([sQuery(id+"F2.wireOp",EDGE,"7QdfqLPk-Ait6-pWA4-Y9kv-QyzDzVu0xvbo.bottom"),sQuery(id+"F2.wireOp",EDGE,"7QdfqLPk-Ait6-pWA4-Y9kv-QyzDzVu0xvbo.left")])]})});
            var Q20;
            Q20=makeQuery(id+"F3.boolean.opBoolean","COPY",EDGE,{"derivedFrom":makeQuery(id+"F3.opExtrude","SWEPT_EDGE",EDGE,{"disambiguationData":[OSD([sQuery(id+"F2.wireOp",EDGE,"98604dad-a57c-4539-978a-768864eea020.top"),sQuery(id+"F2.wireOp",EDGE,"98604dad-a57c-4539-978a-768864eea020.right")])]})});
            var Q21;
            Q21=makeQuery(id+"F3.boolean.opBoolean","COPY",EDGE,{"derivedFrom":makeQuery(id+"F3.opExtrude","SWEPT_EDGE",EDGE,{"disambiguationData":[OSD([sQuery(id+"F2.wireOp",EDGE,"7QdfqLPk-Ait6-pWA4-Y9kv-QyzDzVu0xvbo.bottom"),sQuery(id+"F2.wireOp",EDGE,"7QdfqLPk-Ait6-pWA4-Y9kv-QyzDzVu0xvbo.right")])]})});
            var Q22;
            Q22=makeQuery(id+"F3.boolean.opBoolean","COPY",EDGE,{"derivedFrom":makeQuery(id+"F3.opExtrude","SWEPT_EDGE",EDGE,{"disambiguationData":[OSD([sQuery(id+"F2.wireOp",EDGE,"7QdfqLPk-Ait6-pWA4-Y9kv-QyzDzVu0xvbo.top"),sQuery(id+"F2.wireOp",EDGE,"7QdfqLPk-Ait6-pWA4-Y9kv-QyzDzVu0xvbo.left")])]})});
            var Q23;
            Q23=makeQuery(id+"F3.boolean.opBoolean","COPY",EDGE,{"derivedFrom":makeQuery(id+"F3.opExtrude","SWEPT_EDGE",EDGE,{"disambiguationData":[OSD([sQuery(id+"F2.wireOp",EDGE,"7QdfqLPk-Ait6-pWA4-Y9kv-QyzDzVu0xvbo.top"),sQuery(id+"F2.wireOp",EDGE,"7QdfqLPk-Ait6-pWA4-Y9kv-QyzDzVu0xvbo.right")])]})});
            var Q24;
            Q24=makeQuery(id+"F3.boolean.opBoolean","COPY",EDGE,{"derivedFrom":makeQuery(id+"F3.opExtrude","SWEPT_EDGE",EDGE,{"disambiguationData":[OSD([sQuery(id+"F2.wireOp",EDGE,"E25.top"),sQuery(id+"F2.wireOp",EDGE,"E25.right")])]})});
            var Q25;
            Q25=makeQuery(id+"F3.boolean.opBoolean","COPY",EDGE,{"derivedFrom":makeQuery(id+"F3.opExtrude","SWEPT_EDGE",EDGE,{"disambiguationData":[OSD([sQuery(id+"F2.wireOp",EDGE,"E25.bottom"),sQuery(id+"F2.wireOp",EDGE,"E25.left")])]})});
            var Q26;
            Q26=makeQuery(id+"F3.boolean.opBoolean","COPY",EDGE,{"derivedFrom":makeQuery(id+"F3.opExtrude","SWEPT_EDGE",EDGE,{"disambiguationData":[OSD([sQuery(id+"F2.wireOp",EDGE,"E25.bottom"),sQuery(id+"F2.wireOp",EDGE,"E25.right")])]})});
            var Q27;
            Q27=makeQuery(id+"F3.boolean.opBoolean","COPY",EDGE,{"derivedFrom":makeQuery(id+"F3.opExtrude","SWEPT_EDGE",EDGE,{"disambiguationData":[OSD([sQuery(id+"F2.wireOp",EDGE,"E25.top"),sQuery(id+"F2.wireOp",EDGE,"E25.left")])]})});
            var Q28;
            Q28=makeQuery(id+"F3.boolean.opBoolean","COPY",EDGE,{"derivedFrom":makeQuery(id+"F3.opExtrude","SWEPT_EDGE",EDGE,{"disambiguationData":[OSD([sQuery(id+"F2.wireOp",EDGE,"15a600e8-d899-48a1-9680-452abfeb5a5c56.MirrorCS"),sQuery(id+"F2.wireOp",EDGE,"15a600e8-d899-48a1-9680-452abfeb5a5c59.MirrorCS")])]})});
            var Q29;
            Q29=makeQuery(id+"F3.boolean.opBoolean","COPY",EDGE,{"derivedFrom":makeQuery(id+"F3.opExtrude","SWEPT_EDGE",EDGE,{"disambiguationData":[OSD([sQuery(id+"F2.wireOp",EDGE,"E22.MirrorCS"),sQuery(id+"F2.wireOp",EDGE,"E24.MirrorCS")])]})});
            var Q30;
            Q30=makeQuery(id+"F3.boolean.opBoolean","COPY",EDGE,{"derivedFrom":makeQuery(id+"F3.opExtrude","SWEPT_EDGE",EDGE,{"disambiguationData":[OSD([sQuery(id+"F2.wireOp",EDGE,"15a600e8-d899-48a1-9680-452abfeb5a5c38.MirrorCS"),sQuery(id+"F2.wireOp",EDGE,"15a600e8-d899-48a1-9680-452abfeb5a5c57.MirrorCS")])]})});
            var Q31;
            Q31=makeQuery(id+"F3.boolean.opBoolean","COPY",EDGE,{"derivedFrom":makeQuery(id+"F3.opExtrude","SWEPT_EDGE",EDGE,{"disambiguationData":[OSD([sQuery(id+"F2.wireOp",EDGE,"E21.MirrorCS"),sQuery(id+"F2.wireOp",EDGE,"E23.MirrorCS")])]})});
            var Q32;
            Q32=makeQuery(id+"F3.boolean.opBoolean","COPY",EDGE,{"derivedFrom":makeQuery(id+"F3.opExtrude","SWEPT_EDGE",EDGE,{"disambiguationData":[OSD([sQuery(id+"F2.wireOp",EDGE,"E21.MirrorCS"),sQuery(id+"F2.wireOp",EDGE,"E22.MirrorCS")])]})});
            var Q33;
            Q33=makeQuery(id+"F3.boolean.opBoolean","COPY",EDGE,{"derivedFrom":makeQuery(id+"F3.opExtrude","SWEPT_EDGE",EDGE,{"disambiguationData":[OSD([sQuery(id+"F2.wireOp",EDGE,"15a600e8-d899-48a1-9680-452abfeb5a5c38.MirrorCS"),sQuery(id+"F2.wireOp",EDGE,"15a600e8-d899-48a1-9680-452abfeb5a5c56.MirrorCS")])]})});
            var Q34;
            Q34=makeQuery(id+"F3.boolean.opBoolean","COPY",EDGE,{"derivedFrom":makeQuery(id+"F3.opExtrude","SWEPT_EDGE",EDGE,{"disambiguationData":[OSD([sQuery(id+"F2.wireOp",EDGE,"15a600e8-d899-48a1-9680-452abfeb5a5c57.MirrorCS"),sQuery(id+"F2.wireOp",EDGE,"15a600e8-d899-48a1-9680-452abfeb5a5c59.MirrorCS")])]})});
            var Q35;
            Q35=makeQuery(id+"F3.boolean.opBoolean","COPY",EDGE,{"derivedFrom":makeQuery(id+"F3.opExtrude","SWEPT_EDGE",EDGE,{"disambiguationData":[OSD([sQuery(id+"F2.wireOp",EDGE,"E23.MirrorCS"),sQuery(id+"F2.wireOp",EDGE,"E24.MirrorCS")])]})});
            fillet(context, id + "F6", {"entities" : qUnion([Q0, Q1, Q2, Q3, Q4, Q5, Q6, Q7, Q8, Q9, Q10, Q11, Q12, Q13, Q14, Q15, Q16, Q17, Q18, Q19, Q20, Q21, Q22, Q23, Q24, Q25, Q26, Q27, Q28, Q29, Q30, Q31, Q32, Q33, Q34, Q35]), "radius" : 2 * mm, "tangentPropagation" : true, "allowEdgeOverflow" : false});
        }
        {
            var Q0;
            Q0=makeQuery(id+"F1.opExtrude","CAP_FACE",FACE,{"disambiguationData":[OSD([sQuery(id+"F0.wireOp",EDGE,"E0.0.14"),sQuery(id+"F0.wireOp",EDGE,"E0.0.16"),sQuery(id+"F0.wireOp",EDGE,"E0.0.18"),sQuery(id+"F0.wireOp",EDGE,"E0.0.20"),sQuery(id+"F0.wireOp",EDGE,"E0.0.22"),sQuery(id+"F0.wireOp",EDGE,"E0.0.23"),sQuery(id+"F0.wireOp",EDGE,"E0.0.25"),sQuery(id+"F0.wireOp",EDGE,"E0.0.27"),sQuery(id+"F0.wireOp",EDGE,"E0.0.29"),sQuery(id+"F0.wireOp",EDGE,"E0.0.31"),sQuery(id+"F0.wireOp",EDGE,"E5.MirrorCS"),sQuery(id+"F0.wireOp",EDGE,"E6.MirrorCS"),sQuery(id+"F0.wireOp",EDGE,"E7.MirrorCS"),sQuery(id+"F0.wireOp",EDGE,"E8.MirrorCS"),sQuery(id+"F0.wireOp",EDGE,"E9.MirrorCS"),sQuery(id+"F0.wireOp",EDGE,"E10.MirrorCS"),sQuery(id+"F0.wireOp",EDGE,"E11.MirrorCS"),sQuery(id+"F0.wireOp",EDGE,"E12.MirrorCS"),sQuery(id+"F0.wireOp",EDGE,"E13.MirrorCS"),sQuery(id+"F0.wireOp",EDGE,"E14.MirrorCS")])],"isStart":false});
            var sketch = newSketch(context, id + "F7", { "sketchPlane" : qUnion([Q0])});
            skLineSegment(sketch, "E217.bottom", {"start": v(-20.68, 178.7) * mm, "end": v(-22.28, 178.7) * mm});
            skLineSegment(sketch, "E217.top", {"start": v(-20.68, 174.3) * mm, "end": v(-22.28, 174.3) * mm});
            skLineSegment(sketch, "E217.left", {"start": v(-20.68, 178.7) * mm, "end": v(-20.68, 174.3) * mm});
            skLineSegment(sketch, "E217.right", {"start": v(-22.28, 178.7) * mm, "end": v(-22.28, 174.3) * mm});
            skLineSegment(sketch, "E218", {"start": v(-20.68, 178.7) * mm, "end": v(-22.28, 174.3) * mm, "construction": true});
            skPoint(sketch, "E219", {"position": v(-21.48, 176.5) * mm});
            skLineSegment(sketch, "E220.bottom", {"start": v(-20.68, 174.2) * mm, "end": v(-22.28, 174.2) * mm});
            skLineSegment(sketch, "E220.top", {"start": v(-20.68, 169.8) * mm, "end": v(-22.28, 169.8) * mm});
            skLineSegment(sketch, "E220.left", {"start": v(-20.68, 174.2) * mm, "end": v(-20.68, 169.8) * mm});
            skLineSegment(sketch, "E220.right", {"start": v(-22.28, 174.2) * mm, "end": v(-22.28, 169.8) * mm});
            skLineSegment(sketch, "E221", {"start": v(-20.68, 174.2) * mm, "end": v(-22.28, 169.8) * mm, "construction": true});
            skPoint(sketch, "E222", {"position": v(-21.48, 172) * mm});
            skLineSegment(sketch, "E223.bottom", {"start": v(22.5, 178.6) * mm, "end": v(20.9, 178.6) * mm});
            skLineSegment(sketch, "E223.top", {"start": v(22.5, 174.2) * mm, "end": v(20.9, 174.2) * mm});
            skLineSegment(sketch, "E223.left", {"start": v(22.5, 178.6) * mm, "end": v(22.5, 174.2) * mm});
            skLineSegment(sketch, "E223.right", {"start": v(20.9, 178.6) * mm, "end": v(20.9, 174.2) * mm});
            skLineSegment(sketch, "E224", {"start": v(22.5, 178.6) * mm, "end": v(20.9, 174.2) * mm, "construction": true});
            skPoint(sketch, "E225", {"position": v(21.7, 176.4) * mm});
            skLineSegment(sketch, "E226.bottom", {"start": v(22.5, 174.1) * mm, "end": v(20.9, 174.1) * mm});
            skLineSegment(sketch, "E226.top", {"start": v(22.5, 169.7) * mm, "end": v(20.9, 169.7) * mm});
            skLineSegment(sketch, "E226.left", {"start": v(22.5, 174.1) * mm, "end": v(22.5, 169.7) * mm});
            skLineSegment(sketch, "E226.right", {"start": v(20.9, 174.1) * mm, "end": v(20.9, 169.7) * mm});
            skLineSegment(sketch, "E227", {"start": v(22.5, 174.1) * mm, "end": v(20.9, 169.7) * mm, "construction": true});
            skPoint(sketch, "E228", {"position": v(21.7, 171.9) * mm});
            skLineSegment(sketch, "E229.bottom", {"start": v(22.52, 14.9) * mm, "end": v(20.92, 14.9) * mm});
            skLineSegment(sketch, "E229.top", {"start": v(22.52, 10.5) * mm, "end": v(20.92, 10.5) * mm});
            skLineSegment(sketch, "E229.left", {"start": v(22.52, 14.9) * mm, "end": v(22.52, 10.5) * mm});
            skLineSegment(sketch, "E229.right", {"start": v(20.92, 14.9) * mm, "end": v(20.92, 10.5) * mm});
            skLineSegment(sketch, "E230", {"start": v(22.52, 14.9) * mm, "end": v(20.92, 10.5) * mm, "construction": true});
            skPoint(sketch, "E231", {"position": v(21.72, 12.7) * mm});
            skLineSegment(sketch, "E232.bottom", {"start": v(22.52, 10.4) * mm, "end": v(20.92, 10.4) * mm});
            skLineSegment(sketch, "E232.top", {"start": v(22.52, 6) * mm, "end": v(20.92, 6) * mm});
            skLineSegment(sketch, "E232.left", {"start": v(22.52, 10.4) * mm, "end": v(22.52, 6) * mm});
            skLineSegment(sketch, "E232.right", {"start": v(20.92, 10.4) * mm, "end": v(20.92, 6) * mm});
            skLineSegment(sketch, "E233", {"start": v(22.52, 10.4) * mm, "end": v(20.92, 6) * mm, "construction": true});
            skPoint(sketch, "E234", {"position": v(21.72, 8.2) * mm});
            skLineSegment(sketch, "E235.bottom", {"start": v(-20.48, 14.88) * mm, "end": v(-22.08, 14.88) * mm});
            skLineSegment(sketch, "E235.top", {"start": v(-20.48, 10.48) * mm, "end": v(-22.08, 10.48) * mm});
            skLineSegment(sketch, "E235.left", {"start": v(-20.48, 14.88) * mm, "end": v(-20.48, 10.48) * mm});
            skLineSegment(sketch, "E235.right", {"start": v(-22.08, 14.88) * mm, "end": v(-22.08, 10.48) * mm});
            skLineSegment(sketch, "E236", {"start": v(-20.48, 14.88) * mm, "end": v(-22.08, 10.48) * mm, "construction": true});
            skPoint(sketch, "E237", {"position": v(-21.28, 12.68) * mm});
            skLineSegment(sketch, "E238.bottom", {"start": v(-20.48, 10.38) * mm, "end": v(-22.08, 10.38) * mm});
            skLineSegment(sketch, "E238.top", {"start": v(-20.48, 5.98) * mm, "end": v(-22.08, 5.98) * mm});
            skLineSegment(sketch, "E238.left", {"start": v(-20.48, 10.38) * mm, "end": v(-20.48, 5.98) * mm});
            skLineSegment(sketch, "E238.right", {"start": v(-22.08, 10.38) * mm, "end": v(-22.08, 5.98) * mm});
            skLineSegment(sketch, "E239", {"start": v(-20.48, 10.38) * mm, "end": v(-22.08, 5.98) * mm, "construction": true});
            skPoint(sketch, "E240", {"position": v(-21.28, 8.18) * mm});
            skSolve(sketch);
        }
        {
            var Q0;
            Q0 = qSketchRegion(id + "F7", true);
            extrude(context, id + "F8", {"entities" : qUnion([Q0]), "operationType" : NewBodyOperationType.ADD, "depth" : .6 * mm, "offsetDistance" : 25 * mm});
        }
        {
            var Q0;
            Q0=makeQuery(id+"F1.opExtrude","CAP_FACE",FACE,{"disambiguationData":[OSD([sQuery(id+"F0.wireOp",EDGE,"E0.0.14"),sQuery(id+"F0.wireOp",EDGE,"E0.0.16"),sQuery(id+"F0.wireOp",EDGE,"E0.0.18"),sQuery(id+"F0.wireOp",EDGE,"E0.0.20"),sQuery(id+"F0.wireOp",EDGE,"E0.0.22"),sQuery(id+"F0.wireOp",EDGE,"E0.0.23"),sQuery(id+"F0.wireOp",EDGE,"E0.0.25"),sQuery(id+"F0.wireOp",EDGE,"E0.0.27"),sQuery(id+"F0.wireOp",EDGE,"E0.0.29"),sQuery(id+"F0.wireOp",EDGE,"E0.0.31"),sQuery(id+"F0.wireOp",EDGE,"E5.MirrorCS"),sQuery(id+"F0.wireOp",EDGE,"E6.MirrorCS"),sQuery(id+"F0.wireOp",EDGE,"E7.MirrorCS"),sQuery(id+"F0.wireOp",EDGE,"E8.MirrorCS"),sQuery(id+"F0.wireOp",EDGE,"E9.MirrorCS"),sQuery(id+"F0.wireOp",EDGE,"E10.MirrorCS"),sQuery(id+"F0.wireOp",EDGE,"E11.MirrorCS"),sQuery(id+"F0.wireOp",EDGE,"E12.MirrorCS"),sQuery(id+"F0.wireOp",EDGE,"E13.MirrorCS"),sQuery(id+"F0.wireOp",EDGE,"E14.MirrorCS")])],"isStart":false});
            var sketch = newSketch(context, id + "F9", { "sketchPlane" : qUnion([Q0])});
            skLineSegment(sketch, "E241.bottom", {"start": v(3.5, 118.3) * mm, "end": v(-3.5, 118.3) * mm});
            skLineSegment(sketch, "E241.top", {"start": v(3.5, 125.3) * mm, "end": v(-3.5, 125.3) * mm});
            skLineSegment(sketch, "E241.left", {"start": v(3.5, 118.3) * mm, "end": v(3.5, 125.3) * mm});
            skLineSegment(sketch, "E241.right", {"start": v(-3.5, 118.3) * mm, "end": v(-3.5, 125.3) * mm});
            skPoint(sketch, "E241.middle", {"position": v(0, 121.8) * mm});
            skLineSegment(sketch, "E242.bottom", {"start": v(8.1, 116.3) * mm, "end": v(5.5, 116.3) * mm});
            skLineSegment(sketch, "E242.top", {"start": v(8.1, 122.3) * mm, "end": v(5.5, 122.3) * mm});
            skLineSegment(sketch, "E242.left", {"start": v(8.1, 116.3) * mm, "end": v(8.1, 122.3) * mm});
            skLineSegment(sketch, "E242.right", {"start": v(5.5, 116.3) * mm, "end": v(5.5, 122.3) * mm});
            skPoint(sketch, "E242.middle", {"position": v(6.8, 119.3) * mm});
            skLineSegment(sketch, "E243.bottom", {"start": v(10.25, 110.3) * mm, "end": v(7.35, 110.3) * mm});
            skLineSegment(sketch, "E243.top", {"start": v(10.25, 113.4) * mm, "end": v(7.35, 113.4) * mm});
            skLineSegment(sketch, "E243.left", {"start": v(10.25, 110.3) * mm, "end": v(10.25, 113.4) * mm});
            skLineSegment(sketch, "E243.right", {"start": v(7.35, 110.3) * mm, "end": v(7.35, 113.4) * mm});
            skPoint(sketch, "E243.middle", {"position": v(8.8, 111.85) * mm});
            skLineSegment(sketch, "E244.bottom", {"start": v(2, 110) * mm, "end": v(-2, 110) * mm});
            skLineSegment(sketch, "E244.top", {"start": v(2, 115) * mm, "end": v(-2, 115) * mm});
            skLineSegment(sketch, "E244.left", {"start": v(2, 110) * mm, "end": v(2, 115) * mm});
            skLineSegment(sketch, "E244.right", {"start": v(-2, 110) * mm, "end": v(-2, 115) * mm});
            skPoint(sketch, "E244.middle", {"position": v(0, 112.5) * mm});
            skLineSegment(sketch, "E245.bottom", {"start": v(-5.6, 116) * mm, "end": v(-8.5, 116) * mm});
            skLineSegment(sketch, "E245.top", {"start": v(-5.6, 119.1) * mm, "end": v(-8.5, 119.1) * mm});
            skLineSegment(sketch, "E245.left", {"start": v(-5.6, 116) * mm, "end": v(-5.6, 119.1) * mm});
            skLineSegment(sketch, "E245.right", {"start": v(-8.5, 116) * mm, "end": v(-8.5, 119.1) * mm});
            skPoint(sketch, "E245.middle", {"position": v(-7.05, 117.55) * mm});
            skSolve(sketch);
        }
        {
            var Q0;
            Q0 = qSketchRegion(id + "F9", true);
            extrude(context, id + "F10", {"entities" : qUnion([Q0]), "depth" : 2 * mm, "offsetDistance" : 25 * mm});
        }
    });
